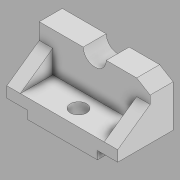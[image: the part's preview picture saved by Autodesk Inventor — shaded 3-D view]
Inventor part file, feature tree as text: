
AUTODESK INVENTOR PART (.ipt)
format: ipt  version: 2020 (Build 240168000, 168)  size: 172,544 bytes
history: native  units: mm
features: extrude x9, sketch x9, other x1
ambient origin geometry x8: Origin, YZ Plane, XZ Plane, XY Plane, X Axis, Y Axis, Z Axis, Center Point
bodies: Body1 (feature_tree)
feature tree (19):
  other  "Sólido1"
  extrude  "Base"  Depth=86.0mm
  extrude  "Orificio_Inferior_Derecho"  Depth=30.0mm
  extrude  "Orificio_Inferior_Izquierdo"  Depth=82.0mm TaperAngle=0.0deg
  extrude  "Medio_Círculo"  Depth=12.0mm
  extrude  "Hueco"  Depth=34.0mm
  extrude  "Círculo"  TaperAngle=0.0deg  [1 undecoded]
  extrude  "Triángulo_Derecho"  Depth=28.0mm
  extrude  "Triángulo_Izquierdo"  Depth=82.0mm
  extrude  "Extrusión11"  Depth=34.0mm
  sketch  "Boceto1"  dims[d0=164.0mm d1=86.0mm]
  sketch  "Boceto2"  dims[d2=82.0mm d3=0.0mm d4=30.0mm]
  sketch  "Boceto3"  dims[d5=12.0mm d6=82.0mm d7=0.0mm]
  sketch  "Boceto5"  dims[d8=30.0mm d9=12.0mm]
  sketch  "Boceto7"  dims[d10=82.0mm d11=0.0mm d15=34.0mm]
  sketch  "Boceto8"  dims[d16=34.0mm d17=0.0mm d23=0.0mm]
  sketch  "Boceto9"  dims[d24=0.0mm d25=28.0mm]
  sketch  "Boceto10"  dims[d26=48.0mm d27=0.0mm d28=82.0mm]
  sketch  "Boceto11"  dims[d29=24.0mm d30=24.0mm d31=28.0mm d32=0.0mm d33=34.0mm d34=20.0mm d35=0.0mm d36=34.0mm d37=20.0mm d38=0.0mm d39=20.0mm d40=62.0mm d41=24.0mm d42=12.0mm d43=34.0mm d44=0.0mm d18=0.872665mm]
note: 1 required parameter value undecoded (feature->parameter linkage not recoverable at this tier; creation-order binding heuristic only, values carry confidence <= 0.55)
